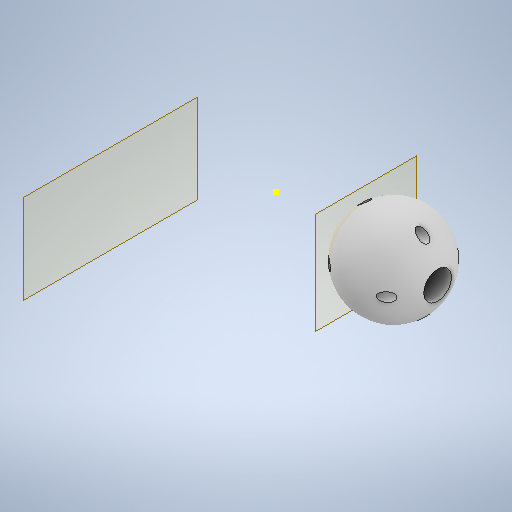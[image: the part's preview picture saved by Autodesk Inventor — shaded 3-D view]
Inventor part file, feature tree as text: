
AUTODESK INVENTOR PART (.ipt)
format: ipt  version: 2025.2 (Build 292293000, 293)  size: 300,544 bytes
history: native  units: in
note: dims shown in document units (in); Inventor stores cm internally (conversion verified against a paired STEP export)
features: sketch x9, plane x2, revolve x1, extrude x1
ambient origin geometry x8: Origin, YZ Plane, XZ Plane, XY Plane, X Axis, Y Axis, Z Axis, Center Point
bodies: Solid1 (feature_tree)
feature tree (13):
  sketch  "Sketch1"  dims[d0=0.3937in d1=90.0deg]
  sketch  "Sketch2"  dims[d4=0.0394in]
  revolve  "Revolution1"  Angle=90.0deg
  plane  "Work Plane1"
  sketch  "Sketch4"  dims[d9=3.937in d10=0.0in]
  sketch  "Sketch5"  dims[d11=-0.1181in]
  extrude  "Extrusion1"  Depth=0.1181in
  sketch  "Sketch7"
  plane  "Work Plane2"
  sketch  "Sketch8"
  sketch  "Sketch3"  dims[d5=1.5748in d7=360.0deg]
  sketch  "Sketch6"
  sketch  "Sketch Circular Pattern1"  dims[d2=-0.5in d3=0.1181in]
